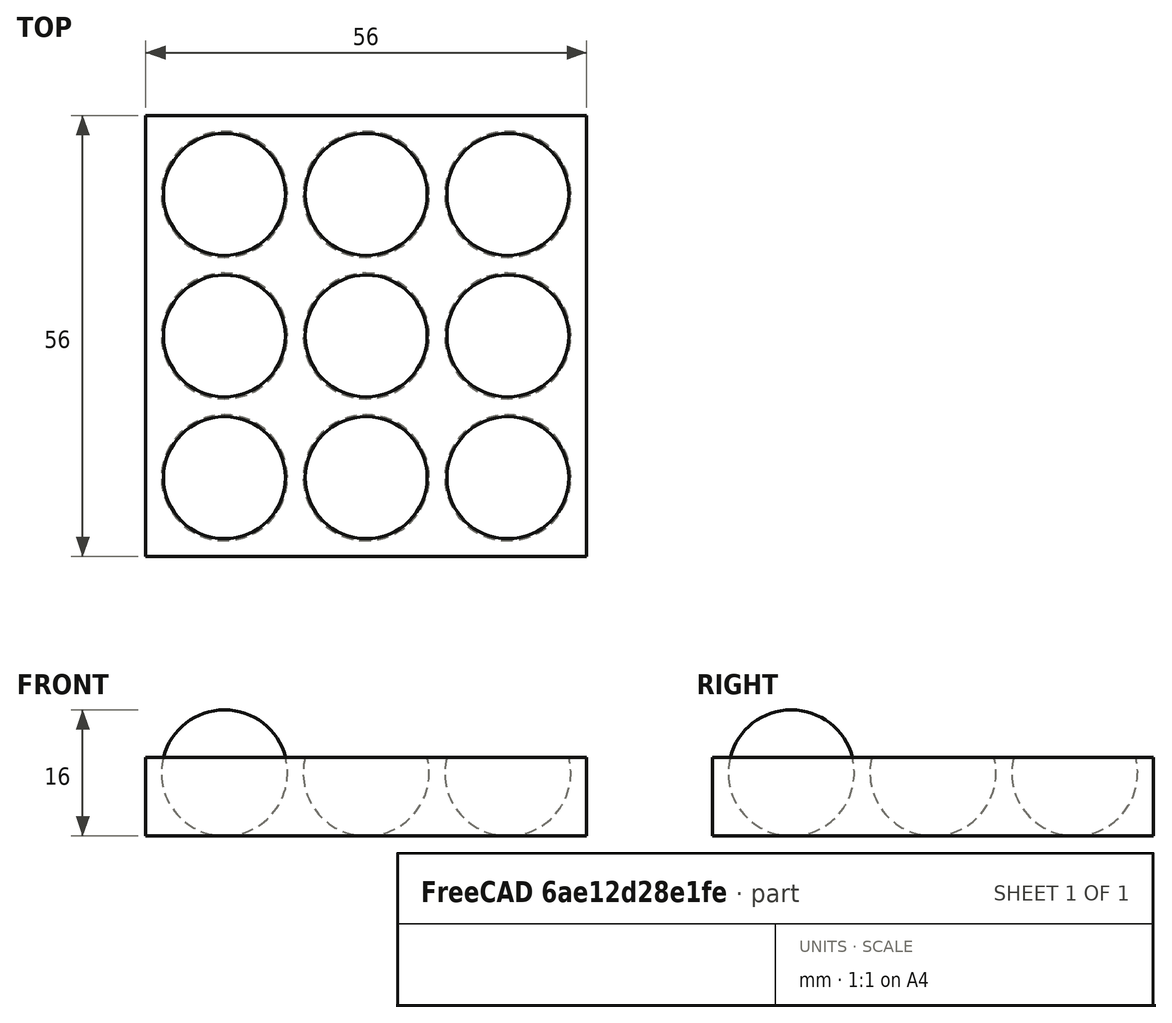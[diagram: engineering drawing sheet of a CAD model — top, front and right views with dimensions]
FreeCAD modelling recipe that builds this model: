
FCSTD DOCUMENT  (FreeCAD 0.21R33694 (Git))
Label: OJT1_T13P03.caniques
License: All rights reserved
LicenseURL: http://en.wikipedia.org/wiki/All_rights_reserved
objects: Part::Sphere×1, Part::FeaturePython×1, Part::Box×1, Part::Cut×1
note: 3 computed .brp shape members not serialized (recipe doc carries the construction recipe); baked Part::Feature solids carry a one-line shape summary decoded from their .brp

FEATURE [Part::Sphere] Sphere  label="Esfera"
  Angle1 = -90
  Angle2 = 90
  Angle3 = 360
  AttacherType = Attacher::AttachEngine3D
  Placement = pos=(0,0,8) rot=(0,0,1;0rad)
  Radius = 8
FEATURE [Part::FeaturePython] Array  # Draft array (typed FeaturePython)
  AlwaysSyncPlacement = false
  Angle = 360
  ArrayType = 0
  Axis = (0,0,1)
  Base = -> Sphere
  Center = (0,0,0)
  Count = 9
  ExpandArray = false
  Fuse = false
  IntervalAxis = (0,0,0)
  IntervalX = (18,0,0)
  IntervalY = (0,18,0)
  IntervalZ = (0,0,100)
  NumberCircles = 3
  NumberPolar = 5
  NumberX = 3
  NumberY = 3
  NumberZ = 1
  PlacementList = 9 placements: [(0,0,8),(0,18,8),(0,36,8),(18,0,8),(18,18,8),(18,36,8),(36,0,8),(36,18,8),(36,36,8)]
  RadialDistance = 50
  ScaleList = (9) [(1,1,1),(1,1,1),(1,1,1),(1,1,1),(1,1,1),(1,1,1),(1,1,1),(1,1,1),(1,1,1)]
  Symmetry = 1
  TangentialDistance = 25
FEATURE [Part::Box] Box  label="Cub"
  AttacherType = Attacher::AttachEngine3D
  Height = 10
  Length = 56
  Placement = pos=(-10,-10,0) rot=(0,0,1;0rad)
  Width = 56
FEATURE [Part::Cut] Cut
  Base = -> Box
  Refine = true
  Tool = -> Array
